# Revit family: IDS_LEGRAND_XL3_HP_160_1
name_source: partatom
category: Modèles génériques
units: mm (PartAtom-declared; Revit-internal decimal feet)

## family parameters
Conserver l'orientation des annotations = Non
Cote de connecteur circulaire = Utiliser le diamètre
Couper avec des vides une fois chargée = Non
Hôte = Mur
Numéro OmniClass = 23.80.30.11.17
Partagée = Non
Peut héberger une armature = Non
Repère de localisation dans la pièce = Non
Titre OmniClass = Distribution Boards and Control Panels
Toujours verticalement = Oui
Type d'élément = Normal

## types (6) — shared parameters
Conditions Générale d'Utilisation = https://assets.legrand.com
Elévation par défaut = 1500 mm  [stored 4.92126 ft]
Fabricant = legrand
Intensité = 160 A
PUISSANCE NOMINALE = 25000 VA
Profondeur porte = 10 mm  [stored 0.0328084 ft]
RAL = 7035
URL = https://www.legrand.fr

## per-type parameters (varying)
| type | A équiper | Bas | Coffret | Encastré | Espace dédié | Haut | Matière 2 | Matière visible | Matière visible 2 | Métal | Plastique | Profondeur | Référence encastrée | Référence à équiper |
| Legrand coffret métal XL3 HP 160 | Non | 25 mm  [stored 0.082021 ft] | Oui | Non | Non | 25 mm  [stored 0.082021 ft] | IDS_METAL | Oui | Non | Oui | Non | 147 mm  [stored 0.482283 ft] | Non | Non |
| Legrand coffret métal XL3 HP 160 à équiper | Oui | 25 mm  [stored 0.082021 ft] | Oui | Non | Non | 25 mm  [stored 0.082021 ft] | IDS_PLASTIQUE | Oui | Non | Oui | Non | 147 mm  [stored 0.482283 ft] | Non | Oui |
| Legrand coffret isolant XL3 HP 160 | Non | 25 mm  [stored 0.082021 ft] | Oui | Non | Non | 25 mm  [stored 0.082021 ft] | IDS_METAL | Non | Oui | Non | Oui | 147 mm  [stored 0.482283 ft] | Non | Non |
| Legrand coffret isolant espace dédié XL3 HP 160 | Non | 25 mm  [stored 0.082021 ft] | Oui | Non | Oui | 25 mm  [stored 0.082021 ft] | IDS_METAL | Non | Oui | Non | Oui | 147 mm  [stored 0.482283 ft] | Non | Non |
| Legrand coffret encastré métal XL3 HP 160 | Non | 73 mm | Non | Oui | Non | 73 mm | IDS_METAL | Oui | Non | Oui | Non | 45 mm  [stored 0.147638 ft] | Oui | Non |
| Legrand coffret encastré espace dédié XL3 HP 160 | Non | 73 mm | Non | Oui | Oui | 73 mm | IDS_METAL | Oui | Non | Oui | Non | 45 mm  [stored 0.147638 ft] | Oui | Non |

note: [stored X ft] marks values corroborated as IEEE doubles in the binary element streams (Revit-internal decimal feet)
